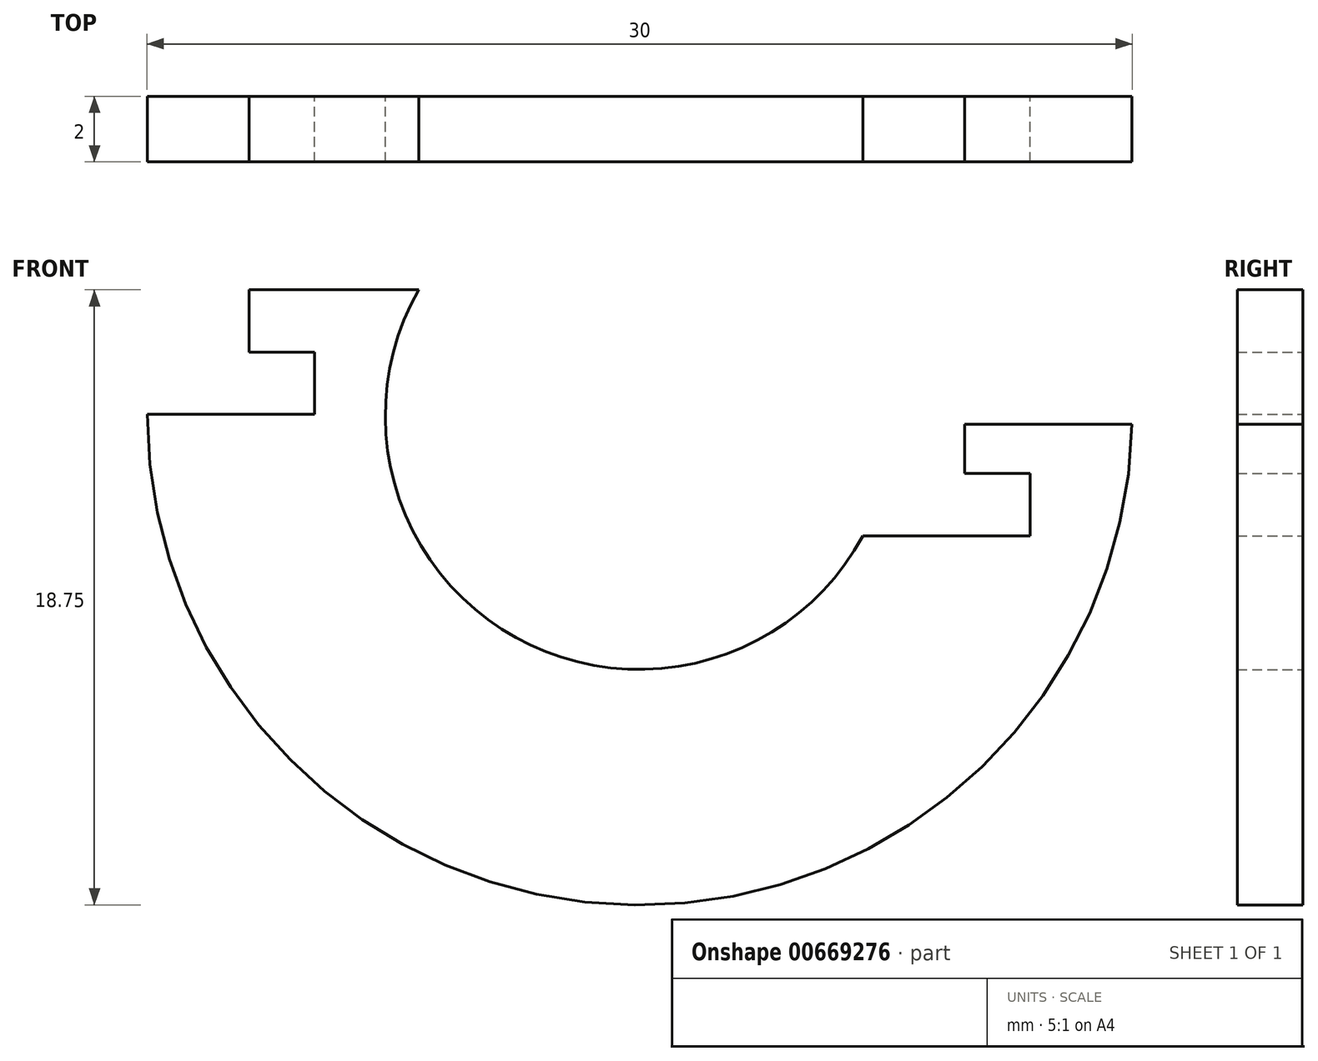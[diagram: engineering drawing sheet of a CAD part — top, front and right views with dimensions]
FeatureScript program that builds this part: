
annotation { "Feature Type Name" : "Feature", "Feature Type Description" : "" }
export const myFeature = defineFeature(function(context is Context, id is Id, definition is map)
    precondition{}
    {
        {
            var Q0;
            Q0=qCreatedBy(makeId("Front.planeOp"),FACE);
            var sketch = newSketch(context, id + "F0", { "sketchPlane" : qUnion([Q0])});
            skLineSegment(sketch, "E0", {"start": v(-15, 0) * mm, "end": v(-9.9, 0) * mm});
            skLineSegment(sketch, "E1", {"start": v(-9.9, 0) * mm, "end": v(-9.9, 1.9) * mm});
            skLineSegment(sketch, "E2", {"start": v(-9.9, 1.9) * mm, "end": v(-11.9, 1.9) * mm});
            skLineSegment(sketch, "E3", {"start": v(-11.9, 1.9) * mm, "end": v(-11.9, 3.8) * mm});
            skLineSegment(sketch, "E4", {"start": v(15, -0.3) * mm, "end": v(9.9, -0.3) * mm});
            skArc(sketch, "E5", {"start": v(-15, 0) * mm, "mid": v(-0.15, -14.95) * mm, "end": v(15, -0.3) * mm});
            skLineSegment(sketch, "E6", {"start": v(-20.11, 0) * mm, "end": v(18.2, 0) * mm, "construction": true});
            skLineSegment(sketch, "E7", {"start": v(0, 13.77) * mm, "end": v(0, -15.5) * mm, "construction": true});
            skLineSegment(sketch, "E8", {"start": v(9.9, -0.3) * mm, "end": v(9.9, -1.8) * mm});
            skLineSegment(sketch, "E9", {"start": v(9.9, -1.8) * mm, "end": v(11.9, -1.8) * mm});
            skLineSegment(sketch, "E10", {"start": v(-6.72, 3.8) * mm, "end": v(-11.9, 3.8) * mm});
            skLineSegment(sketch, "E11", {"start": v(11.9, -1.8) * mm, "end": v(11.9, -3.7) * mm});
            skLineSegment(sketch, "E12", {"start": v(11.9, -3.7) * mm, "end": v(6.8, -3.7) * mm});
            skArc(sketch, "E13", {"start": v(-6.72, 3.8) * mm, "mid": v(-3.77, -6.8) * mm, "end": v(6.8, -3.7) * mm});
            skSolve(sketch);
        }
        {
            var Q0;
            Q0 = qSketchRegion(id + "F0", true);
            extrude(context, id + "F1", {"entities" : qUnion([Q0]), "depth" : 2 * mm, "offsetDistance" : 25 * mm});
        }
    });
